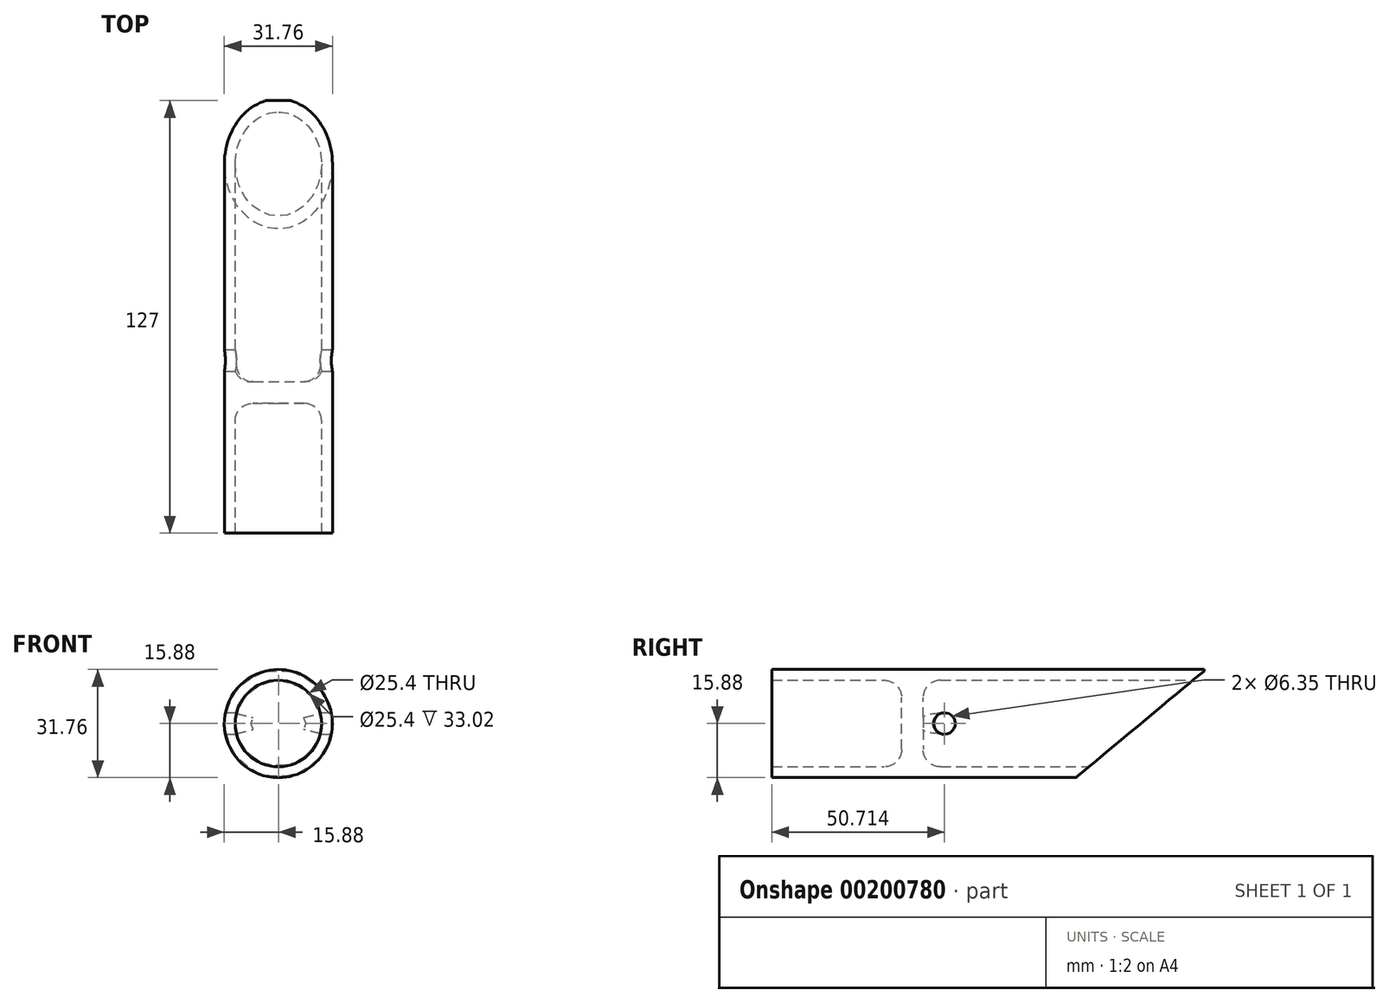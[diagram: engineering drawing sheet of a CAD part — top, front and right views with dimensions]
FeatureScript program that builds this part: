
annotation { "Feature Type Name" : "Feature", "Feature Type Description" : "" }
export const myFeature = defineFeature(function(context is Context, id is Id, definition is map)
    precondition{}
    {
        {
            var Q0;
            Q0=qCreatedBy(makeId("Front.planeOp"),FACE);
            var sketch = newSketch(context, id + "F0", { "sketchPlane" : qUnion([Q0])});
            skCircle(sketch, "E0", {"center": v(0, 0) * mm, "radius": 15.88 * mm});
            skLineSegment(sketch, "E1", {"start": v(-6.87, 14.31) * mm, "end": v(-5.33, 11.54) * mm});
            skCircle(sketch, "E2", {"center": v(0, 0) * mm, "radius": 12.7 * mm});
            skSolve(sketch);
        }
        {
            var Q0;
            Q0 = qSketchRegion(id + "F0", true);
            extrude(context, id + "F1", {"entities" : qUnion([Q0]), "depth" : 127 * mm});
        }
        {
            var Q0;
            Q0=qCreatedBy(makeId("Right.planeOp"),FACE);
            var sketch = newSketch(context, id + "F2", { "sketchPlane" : qUnion([Q0])});
            skLineSegment(sketch, "E3", {"start": v(0, -16.2) * mm, "end": v(-38.1, -16.2) * mm});
            skLineSegment(sketch, "E4", {"start": v(-38.1, -16.2) * mm, "end": v(0, 15.47) * mm});
            skLineSegment(sketch, "E5", {"start": v(0, 15.47) * mm, "end": v(0, -16.2) * mm});
            skPoint(sketch, "E6.center.orphan", {"position": v(-61.94, 0) * mm});
            skLineSegment(sketch, "E7", {"start": v(-127.09, 0) * mm, "end": v(-76.29, 0) * mm});
            skCircle(sketch, "E8", {"center": v(-76.29, 0) * mm, "radius": 3.18 * mm});
            skSolve(sketch);
        }
        {
            var Q0;
            Q0 = qSketchRegion(id + "F2", true);
            extrude(context, id + "F3", {"entities" : qUnion([Q0]), "operationType" : NewBodyOperationType.REMOVE, "oppositeDirection" : true, "depth" : 25.4 * mm, "hasSecondDirection" : true, "secondDirectionOppositeDirection" : false, "secondDirectionDepth" : 25.4 * mm});
        }
        {
            var Q0;
            Q0=qCreatedBy(makeId("Front.planeOp"),FACE);
            cPlane(context, id + "F4", {"entities" : qUnion([Q0]), "cplaneType" : CPlaneType.OFFSET, "offset" : 82.55 * mm, "width" : 152.4 * mm, "height" : 152.4 * mm});
        }
        {
            var Q0;
            Q0=qCreatedBy(id+"F4.planeOp",FACE);
            var sketch = newSketch(context, id + "F5", { "sketchPlane" : qUnion([Q0])});
            skCircle(sketch, "E9", {"center": v(0, 0) * mm, "radius": 12.7 * mm});
            skSolve(sketch);
        }
        {
            var Q0;
            Q0 = qSketchRegion(id + "F5", true);
            extrude(context, id + "F6", {"entities" : qUnion([Q0]), "operationType" : NewBodyOperationType.ADD, "depth" : 6.35 * mm});
        }
        {
            var Q0;
            Q0=makeQuery(id+"F6.opExtrude","CAP_FACE",FACE,{"disambiguationData":[OSD([sQuery(id+"F5.wireOp",EDGE,"E9")])],"isStart":true});
            fillet(context, id + "F7", {"entities" : qUnion([Q0]), "radius" : 5.08 * mm, "tangentPropagation" : true, "allowEdgeOverflow" : false});
        }
        {
            var Q0;
            Q0=makeQuery(id+"F6.opExtrude","CAP_FACE",FACE,{"disambiguationData":[OSD([sQuery(id+"F5.wireOp",EDGE,"E9")])],"isStart":false});
            fillet(context, id + "F8", {"entities" : qUnion([Q0]), "radius" : 5.08 * mm, "tangentPropagation" : true, "allowEdgeOverflow" : false});
        }
    });
